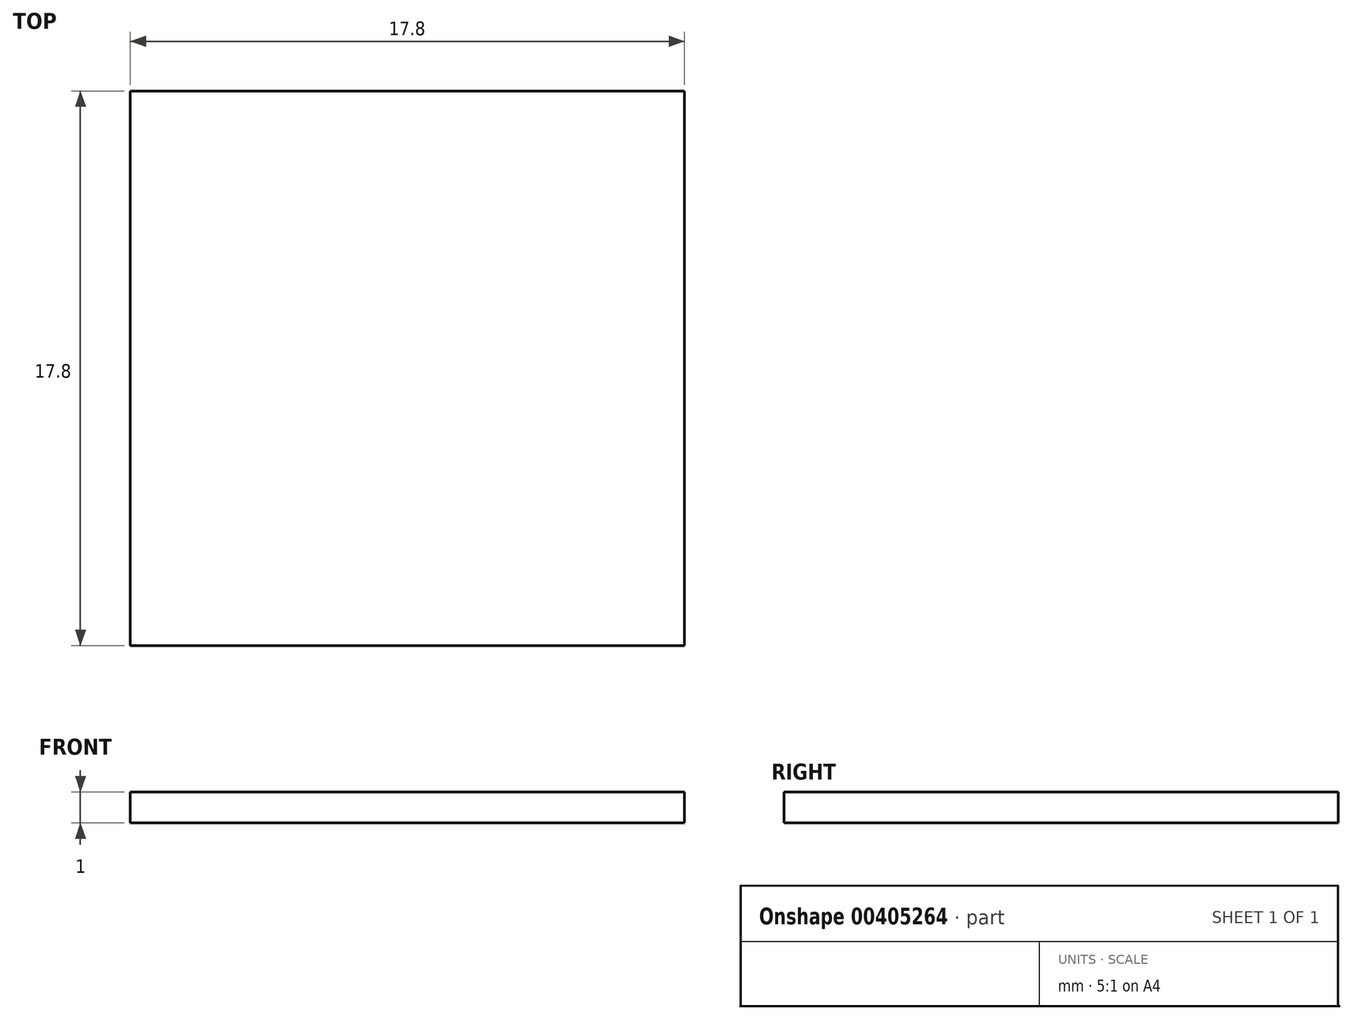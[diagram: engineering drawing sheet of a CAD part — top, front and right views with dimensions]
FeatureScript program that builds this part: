
annotation { "Feature Type Name" : "Feature", "Feature Type Description" : "" }
export const myFeature = defineFeature(function(context is Context, id is Id, definition is map)
    precondition{}
    {
        {
            var Q0;
            Q0=qCreatedBy(makeId("Top.planeOp"),FACE);
            var sketch = newSketch(context, id + "F0", { "sketchPlane" : qUnion([Q0])});
            skLineSegment(sketch, "E0.bottom", {"start": v(8.9, -8.9) * mm, "end": v(-8.9, -8.9) * mm});
            skLineSegment(sketch, "E0.top", {"start": v(8.9, 8.9) * mm, "end": v(-8.9, 8.9) * mm});
            skLineSegment(sketch, "E0.left", {"start": v(8.9, -8.9) * mm, "end": v(8.9, 8.9) * mm});
            skLineSegment(sketch, "E0.right", {"start": v(-8.9, -8.9) * mm, "end": v(-8.9, 8.9) * mm});
            skPoint(sketch, "E0.middle", {"position": v(0, 0) * mm});
            skSolve(sketch);
        }
        {
            var Q0;
            Q0 = qSketchRegion(id + "F0", true);
            extrude(context, id + "F1", {"entities" : qUnion([Q0]), "depth" : 1 * mm});
        }
    });
